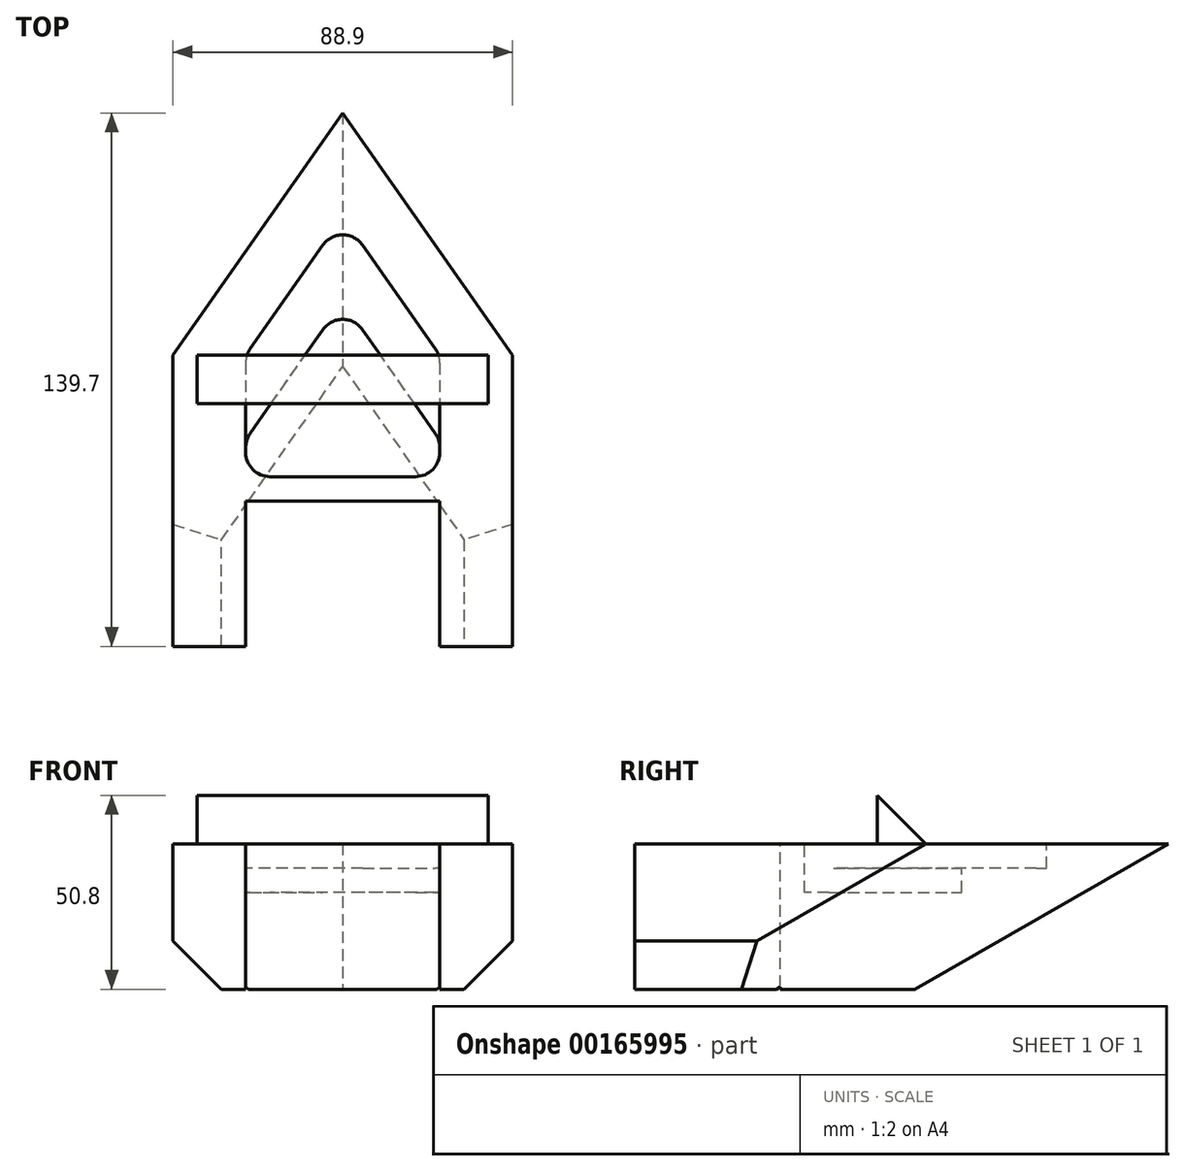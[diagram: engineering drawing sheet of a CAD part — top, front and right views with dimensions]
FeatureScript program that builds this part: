
annotation { "Feature Type Name" : "Feature", "Feature Type Description" : "" }
export const myFeature = defineFeature(function(context is Context, id is Id, definition is map)
    precondition{}
    {
        {
            var Q0;
            Q0=qCreatedBy(makeId("Top.planeOp"),FACE);
            var sketch = newSketch(context, id + "F0", { "sketchPlane" : qUnion([Q0])});
            skLineSegment(sketch, "E0.bottom", {"start": v(-44.45, 0) * mm, "end": v(44.45, 0) * mm});
            skLineSegment(sketch, "E0.top", {"start": v(-44.45, -76.22) * mm, "end": v(-25.4, -76.22) * mm});
            skLineSegment(sketch, "E0.left", {"start": v(-44.45, 0) * mm, "end": v(-44.45, -76.22) * mm});
            skLineSegment(sketch, "E0.right", {"start": v(44.45, 0) * mm, "end": v(44.45, -76.22) * mm});
            skLineSegment(sketch, "E1", {"start": v(-44.45, 0) * mm, "end": v(0, 63.48) * mm});
            skLineSegment(sketch, "E2", {"start": v(0, 63.48) * mm, "end": v(44.45, 0) * mm});
            skLineSegment(sketch, "E3.top", {"start": v(-25.4, -38.12) * mm, "end": v(25.4, -38.12) * mm});
            skLineSegment(sketch, "E3.left", {"start": v(-25.4, -76.22) * mm, "end": v(-25.4, -38.12) * mm});
            skLineSegment(sketch, "E3.right", {"start": v(25.4, -76.22) * mm, "end": v(25.4, -38.12) * mm});
            skLineSegment(sketch, "E4", {"start": v(0, 0) * mm, "end": v(0, -38.12) * mm, "construction": true});
            skLineSegment(sketch, "E5.trimOffspring", {"start": v(25.4, -76.22) * mm, "end": v(44.45, -76.22) * mm});
            skSolve(sketch);
        }
        {
            var Q0;
            Q0 = qSketchRegion(id + "F0", true);
            extrude(context, id + "F1", {"entities" : qUnion([Q0]), "oppositeDirection" : true, "depth" : 38.1 * mm});
        }
        {
            var Q0;
            Q0=makeQuery(id+"F1.opExtrude","CAP_EDGE",EDGE,{"disambiguationData":[OSD([sQuery(id+"F0.wireOp",EDGE,"E2")])],"isStart":false});
            var Q1;
            Q1=makeQuery(id+"F1.opExtrude","CAP_EDGE",EDGE,{"disambiguationData":[OSD([sQuery(id+"F0.wireOp",EDGE,"E1")])],"isStart":false});
            chamfer(context, id + "F2", {"entities" : qUnion([Q0, Q1]), "width" : 38.1 * mm, "tangentPropagation" : true});
        }
        {
            var Q0;
            Q0=makeQuery(id+"F1.opExtrude","CAP_EDGE",EDGE,{"disambiguationData":[OSD([sQuery(id+"F0.wireOp",EDGE,"E0.right")])],"isStart":false});
            var Q1;
            Q1=makeQuery(id+"F1.opExtrude","CAP_EDGE",EDGE,{"disambiguationData":[OSD([sQuery(id+"F0.wireOp",EDGE,"E0.left")])],"isStart":false});
            chamfer(context, id + "F3", {"entities" : qUnion([Q0, Q1]), "width" : 12.7 * mm, "tangentPropagation" : true});
        }
        {
            var Q0;
            Q0=qCreatedBy(makeId("Top.planeOp"),FACE);
            var sketch = newSketch(context, id + "F4", { "sketchPlane" : qUnion([Q0])});
            skLineSegment(sketch, "E6", {"start": v(-5.2, 28.85) * mm, "end": v(-24.25, 1.64) * mm});
            skLineSegment(sketch, "E7", {"start": v(-25.4, -2) * mm, "end": v(-25.4, -25.42) * mm});
            skLineSegment(sketch, "E8", {"start": v(-19.05, -31.77) * mm, "end": v(0, -31.77) * mm});
            skLineSegment(sketch, "E9", {"start": v(0, 36.27) * mm, "end": v(0, -31.77) * mm, "construction": true});
            skLineSegment(sketch, "E10.MirrorCS", {"start": v(5.2, 28.85) * mm, "end": v(24.25, 1.64) * mm});
            skLineSegment(sketch, "E11.MirrorCS", {"start": v(25.4, -2) * mm, "end": v(25.4, -25.42) * mm});
            skLineSegment(sketch, "E12.MirrorCS", {"start": v(19.05, -31.77) * mm, "end": v(0, -31.77) * mm});
            skPoint(sketch, "E13.visualSharp", {"position": v(0, 36.27) * mm});
            skArc(sketch, "E13.filletArc", {"start": v(5.2, 28.85) * mm, "mid": v(0, 31.55) * mm, "end": v(-5.2, 28.85) * mm});
            skPoint(sketch, "E14.visualSharp", {"position": v(-25.4, 0) * mm});
            skArc(sketch, "E14.filletArc", {"start": v(-24.25, 1.64) * mm, "mid": v(-25.1, -0.1) * mm, "end": v(-25.4, -2) * mm});
            skPoint(sketch, "E15.visualSharp", {"position": v(-25.4, -31.77) * mm});
            skArc(sketch, "E15.filletArc", {"start": v(-25.4, -25.42) * mm, "mid": v(-23.54, -29.9) * mm, "end": v(-19.05, -31.77) * mm});
            skPoint(sketch, "E16.visualSharp", {"position": v(25.4, -31.77) * mm});
            skArc(sketch, "E16.filletArc", {"start": v(19.05, -31.77) * mm, "mid": v(23.54, -29.9) * mm, "end": v(25.4, -25.42) * mm});
            skPoint(sketch, "E17.visualSharp", {"position": v(25.4, 0) * mm});
            skArc(sketch, "E17.filletArc", {"start": v(25.4, -2) * mm, "mid": v(25.1, -0.1) * mm, "end": v(24.25, 1.64) * mm});
            skSolve(sketch);
        }
        {
            var Q0;
            Q0 = qSketchRegion(id + "F4", true);
            extrude(context, id + "F5", {"entities" : qUnion([Q0]), "operationType" : NewBodyOperationType.REMOVE, "oppositeDirection" : true, "depth" : 6.35 * mm});
        }
        {
            var Q0;
            Q0=qCreatedBy(makeId("Right.planeOp"),FACE);
            var sketch = newSketch(context, id + "F6", { "sketchPlane" : qUnion([Q0])});
            skLineSegment(sketch, "E18", {"start": v(-12.7, 0) * mm, "end": v(-12.7, 12.7) * mm});
            skLineSegment(sketch, "E19", {"start": v(-12.7, 0) * mm, "end": v(0, 0) * mm});
            skLineSegment(sketch, "E20", {"start": v(0, 0) * mm, "end": v(-12.7, 12.7) * mm});
            skSolve(sketch);
        }
        {
            var Q0;
            Q0=qCreatedBy(makeId("Top.planeOp"),FACE);
            var sketch = newSketch(context, id + "F7", { "sketchPlane" : qUnion([Q0])});
            skLineSegment(sketch, "E21", {"start": v(0, -31.77) * mm, "end": v(-19.05, -31.77) * mm});
            skLineSegment(sketch, "E22", {"start": v(-25.4, -25.42) * mm, "end": v(-25.4, -24.14) * mm});
            skLineSegment(sketch, "E23", {"start": v(-24.25, -20.5) * mm, "end": v(-5.2, 6.7) * mm});
            skLineSegment(sketch, "E24", {"start": v(0, 14.13) * mm, "end": v(0, -31.77) * mm, "construction": true});
            skLineSegment(sketch, "E25.MirrorCS", {"start": v(24.25, -20.5) * mm, "end": v(5.2, 6.7) * mm});
            skLineSegment(sketch, "E26.MirrorCS", {"start": v(25.4, -25.42) * mm, "end": v(25.4, -24.14) * mm});
            skLineSegment(sketch, "E27.MirrorCS", {"start": v(0, -31.77) * mm, "end": v(19.05, -31.77) * mm});
            skPoint(sketch, "E28.visualSharp", {"position": v(0, 14.13) * mm});
            skArc(sketch, "E28.filletArc", {"start": v(5.2, 6.7) * mm, "mid": v(0, 9.41) * mm, "end": v(-5.2, 6.7) * mm});
            skPoint(sketch, "E29.visualSharp", {"position": v(-25.4, -22.14) * mm});
            skArc(sketch, "E29.filletArc", {"start": v(-24.25, -20.5) * mm, "mid": v(-25.1, -22.23) * mm, "end": v(-25.4, -24.14) * mm});
            skPoint(sketch, "E30.visualSharp", {"position": v(-25.4, -31.77) * mm});
            skArc(sketch, "E30.filletArc", {"start": v(-25.4, -25.42) * mm, "mid": v(-23.54, -29.9) * mm, "end": v(-19.05, -31.77) * mm});
            skPoint(sketch, "E31.visualSharp", {"position": v(25.4, -31.77) * mm});
            skArc(sketch, "E31.filletArc", {"start": v(19.05, -31.77) * mm, "mid": v(23.54, -29.9) * mm, "end": v(25.4, -25.42) * mm});
            skPoint(sketch, "E32.visualSharp", {"position": v(25.4, -22.14) * mm});
            skArc(sketch, "E32.filletArc", {"start": v(25.4, -24.14) * mm, "mid": v(25.1, -22.23) * mm, "end": v(24.25, -20.5) * mm});
            skSolve(sketch);
        }
        {
            var Q0;
            Q0 = qSketchRegion(id + "F7", true);
            extrude(context, id + "F8", {"entities" : qUnion([Q0]), "operationType" : NewBodyOperationType.REMOVE, "oppositeDirection" : true, "depth" : 12.7 * mm});
        }
        {
            var Q0;
            Q0 = qSketchRegion(id + "F6", true);
            extrude(context, id + "F9", {"entities" : qUnion([Q0]), "operationType" : NewBodyOperationType.ADD, "endBound" : BoundingType.SYMMETRIC, "depth" : 76.2 * mm});
        }
    });
